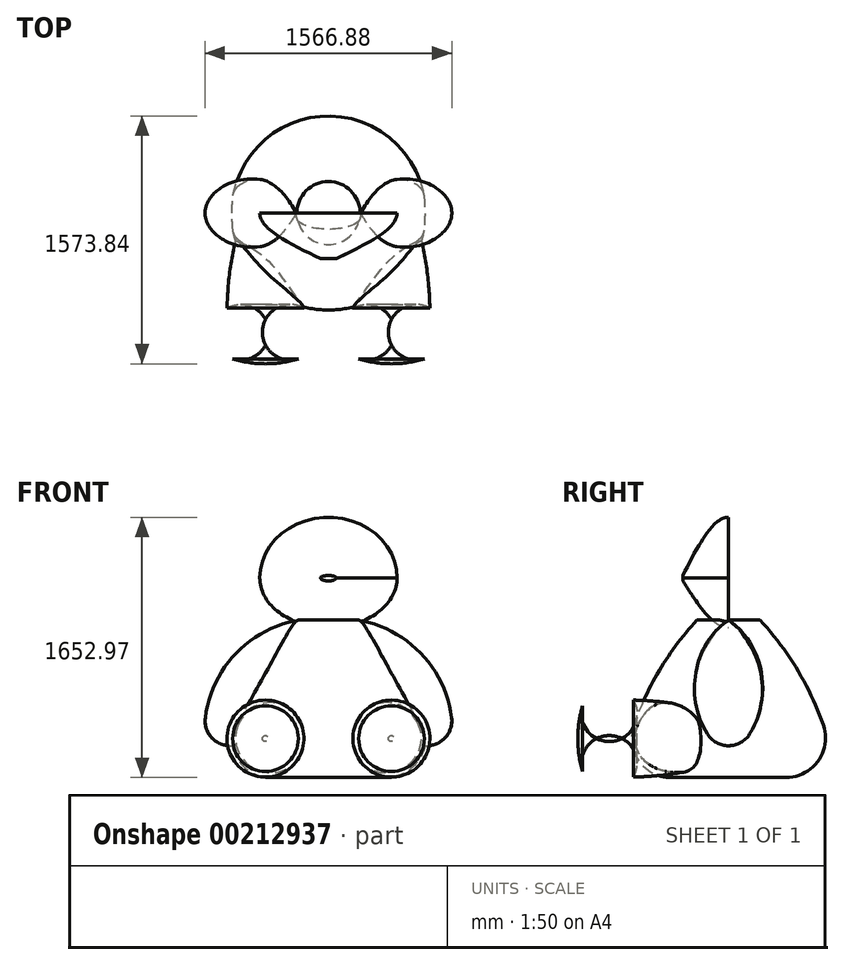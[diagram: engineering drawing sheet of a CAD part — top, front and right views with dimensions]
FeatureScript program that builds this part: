
annotation { "Feature Type Name" : "Feature", "Feature Type Description" : "" }
export const myFeature = defineFeature(function(context is Context, id is Id, definition is map)
    precondition{}
    {
        {
            var Q0;
            Q0=qCreatedBy(makeId("Front.planeOp"),FACE);
            var sketch = newSketch(context, id + "F0", { "sketchPlane" : qUnion([Q0])});
            skLineSegment(sketch, "E0", {"start": v(0, 0) * mm, "end": v(0, 1000) * mm});
            skLineSegment(sketch, "E1", {"start": v(0, 1000) * mm, "end": v(200, 1000) * mm});
            skArc(sketch, "E2", {"start": v(602.1, 332.8) * mm, "mid": v(435.33, 687.06) * mm, "end": v(200, 1000) * mm});
            skLineSegment(sketch, "E3", {"start": v(0, 0) * mm, "end": v(366.2, 0) * mm});
            skArc(sketch, "E4.filletArc", {"start": v(366.2, 0) * mm, "mid": v(570.17, 105.43) * mm, "end": v(602.1, 332.8) * mm});
            skSolve(sketch);
        }
        {
            var Q0;
            Q0 = qSketchRegion(id + "F0", true);
            var Q1;
            Q1=sQuery(id+"F0.wireOp",EDGE,"E0");
            revolve(context, id + "F1", {"surfaceOperationType" : NewSurfaceOperationType.NEW, "entities" : qUnion([Q0]), "axis" : qUnion([Q1]), "revolveType" : RevolveType.FULL});
        }
        {
            var Q0;
            Q0=qCreatedBy(makeId("Right.planeOp"),FACE);
            cPlane(context, id + "F2", {"entities" : qUnion([Q0]), "cplaneType" : CPlaneType.OFFSET, "offset" : 400 * mm, "oppositeDirection" : true, "width" : 150 * mm, "height" : 150 * mm});
        }
        {
            var Q0;
            Q0=qCreatedBy(id+"F2.planeOp",FACE);
            var sketch = newSketch(context, id + "F3", { "sketchPlane" : qUnion([Q0])});
            skArc(sketch, "E5", {"start": v(-603.54, 491.65) * mm, "mid": v(-776.99, 580.62) * mm, "end": v(-926.85, 455.96) * mm});
            skLineSegment(sketch, "E6", {"start": v(157.9, 247.43) * mm, "end": v(-957.63, 247.43) * mm});
            skArc(sketch, "E7", {"start": v(-926.85, 455.96) * mm, "mid": v(-949.9, 352.83) * mm, "end": v(-957.63, 247.43) * mm});
            skArc(sketch, "E8", {"start": v(77.76, 362.47) * mm, "mid": v(-257.5, 455.5) * mm, "end": v(-603.54, 491.65) * mm});
            skArc(sketch, "E9", {"start": v(157.9, 247.43) * mm, "mid": v(135.89, 317.53) * mm, "end": v(77.76, 362.47) * mm});
            skPoint(sketch, "E10.MirrorCS.end.orphan", {"position": v(-558.69, 91.01) * mm});
            skPoint(sketch, "E10.MirrorCS.start.orphan", {"position": v(77.76, 132.4) * mm});
            skSolve(sketch);
        }
        {
            var Q0;
            Q0 = qSketchRegion(id + "F3", true);
            var Q1;
            Q1=sQuery(id+"F3.wireOp",EDGE,"E6");
            revolve(context, id + "F4", {"surfaceOperationType" : NewSurfaceOperationType.NEW, "entities" : qUnion([Q0]), "axis" : qUnion([Q1]), "revolveType" : RevolveType.FULL});
        }
        {
            var Q0;
            Q0=qCreatedBy(makeId("Right.planeOp"),FACE);
            var sketch = newSketch(context, id + "F5", { "sketchPlane" : qUnion([Q0])});
            skLineSegment(sketch, "E11.bottom", {"start": v(0, 0) * mm, "end": v(-1049.03, 0) * mm});
            skLineSegment(sketch, "E11.top", {"start": v(0, -101.42) * mm, "end": v(-1049.03, -101.42) * mm});
            skLineSegment(sketch, "E11.left", {"start": v(0, 0) * mm, "end": v(0, -101.42) * mm});
            skLineSegment(sketch, "E11.right", {"start": v(-1049.03, 0) * mm, "end": v(-1049.03, -101.42) * mm});
            skSolve(sketch);
        }
        {
            var Q0;
            Q0 = qSketchRegion(id + "F5", true);
            extrude(context, id + "F6", {"entities" : qUnion([Q0]), "operationType" : NewBodyOperationType.REMOVE, "oppositeDirection" : true, "depth" : 959 * mm, "offsetDistance" : 25 * mm});
        }
        {
            var Q0;
            Q0=qCreatedBy(makeId("Front.planeOp"),FACE);
            var sketch = newSketch(context, id + "F7", { "sketchPlane" : qUnion([Q0])});
            skArc(sketch, "E12", {"start": v(-200.56, 997.86) * mm, "mid": v(-591.95, 783.7) * mm, "end": v(-782.2, 380.14) * mm});
            skArc(sketch, "E13", {"start": v(-782.2, 380.14) * mm, "mid": v(-769.1, 294.45) * mm, "end": v(-712.86, 228.49) * mm});
            skLineSegment(sketch, "E14", {"start": v(-712.86, 228.49) * mm, "end": v(-200.56, 997.86) * mm});
            skSolve(sketch);
        }
        {
            var Q0;
            Q0 = qSketchRegion(id + "F7", true);
            var Q1;
            Q1=sQuery(id+"F7.wireOp",EDGE,"E14");
            revolve(context, id + "F8", {"surfaceOperationType" : NewSurfaceOperationType.NEW, "entities" : qUnion([Q0]), "axis" : qUnion([Q1]), "revolveType" : RevolveType.FULL});
        }
        {
            var Q0;
            Q0=qCreatedBy(makeId("Front.planeOp"),FACE);
            var sketch = newSketch(context, id + "F9", { "sketchPlane" : qUnion([Q0])});
            skEllipticalArc(sketch, "E15", {});
            skLineSegment(sketch, "E16", {"start": v(-436.2, 1268.53) * mm, "end": v(436.2, 1268.53) * mm, "construction": true});
            skEllipticalArc(sketch, "E17", {});
            const initialGuessF9  = {"E15": [0, 1.2685285806655884, 0, -1, 0.3844454288482666, 0.43619541449303456, 1.5707963267948966, 4.71238898038469], "E17": [0, 1.2685285806655884, -1, 0, 0.43619541449303456, 0.3168308966319093, 0, 3.141592653589793]};
            skSetInitialGuess(sketch, initialGuessF9);
            skSolve(sketch);
        }
        {
            var Q0;
            Q0=qCreatedBy(makeId("Front.planeOp"),FACE);
            cPlane(context, id + "F10", {"entities" : qUnion([Q0]), "cplaneType" : CPlaneType.OFFSET, "offset" : 290 * mm, "width" : 150 * mm, "height" : 150 * mm});
        }
        {
            var Q0;
            Q0=qCreatedBy(id+"F10.planeOp",FACE);
            var sketch = newSketch(context, id + "F11", { "sketchPlane" : qUnion([Q0])});
            skPoint(sketch, "E18.0", {"position": v(0, 1268.53) * mm});
            skEllipticalArc(sketch, "E19", {});
            skLineSegment(sketch, "E20", {"start": v(-50, 1268.53) * mm, "end": v(50, 1268.53) * mm, "construction": true});
            skEllipticalArc(sketch, "E21", {});
            const initialGuessF11  = {"E19": [0, 1.2685285806655884, 0, 1, 0.015, 0.05, 4.71238898038469, 1.5707963267948966], "E21": [0, 1.2685285806655884, -1, 0, 0.05, 0.02, 0, 3.141592653589793]};
            skSetInitialGuess(sketch, initialGuessF11);
            skSolve(sketch);
        }
        {
            var Q0;
            Q0=makeQuery(id+"F9.imprint","IMPRINT",FACE,{"disambiguationData":[TD([[makeQuery(id+"F9.imprint","IMPRINT",EDGE,{"derivedFrom":sQuery(id+"F9.wireOp",EDGE,"E15")}),1.0]])]});
            var Q1;
            Q1=makeQuery(id+"F11.imprint","IMPRINT",FACE,{"disambiguationData":[TD([[makeQuery(id+"F11.imprint","IMPRINT",EDGE,{"derivedFrom":sQuery(id+"F11.wireOp",EDGE,"E19")}),1.0]])]});
            loft(context, id + "F12", {"startCondition" : LoftEndDerivativeType.NORMAL_TO_PROFILE, "startMagnitude" : 1, "sheetProfilesArray" : [{ "sheetProfileEntities" : qUnion([Q0]) }, { "sheetProfileEntities" : qUnion([Q1]) }]});
        }
        {
            var Q0;
            Q0=makeQuery(id+"F4.opRevolve","SWEPT_BODY",BODY,{"disambiguationData":[OSD([sQuery(id+"F3.wireOp",EDGE,"E5"),sQuery(id+"F3.wireOp",EDGE,"E6"),sQuery(id+"F3.wireOp",EDGE,"E7"),sQuery(id+"F3.wireOp",EDGE,"E8"),sQuery(id+"F3.wireOp",EDGE,"E9")])]});
            var Q1;
            Q1=makeQuery(id+"F8.opRevolve","SWEPT_BODY",BODY,{"disambiguationData":[OSD([sQuery(id+"F7.wireOp",EDGE,"E12"),sQuery(id+"F7.wireOp",EDGE,"E13"),sQuery(id+"F7.wireOp",EDGE,"E14")])]});
            var Q2;
            Q2=qCreatedBy(makeId("Right.planeOp"),FACE);
            mirror(context, id + "F13", {"operationType" : NewBodyOperationType.ADD, "entities" : qUnion([Q0, Q1]), "mirrorPlane" : qUnion([Q2])});
        }
    });
